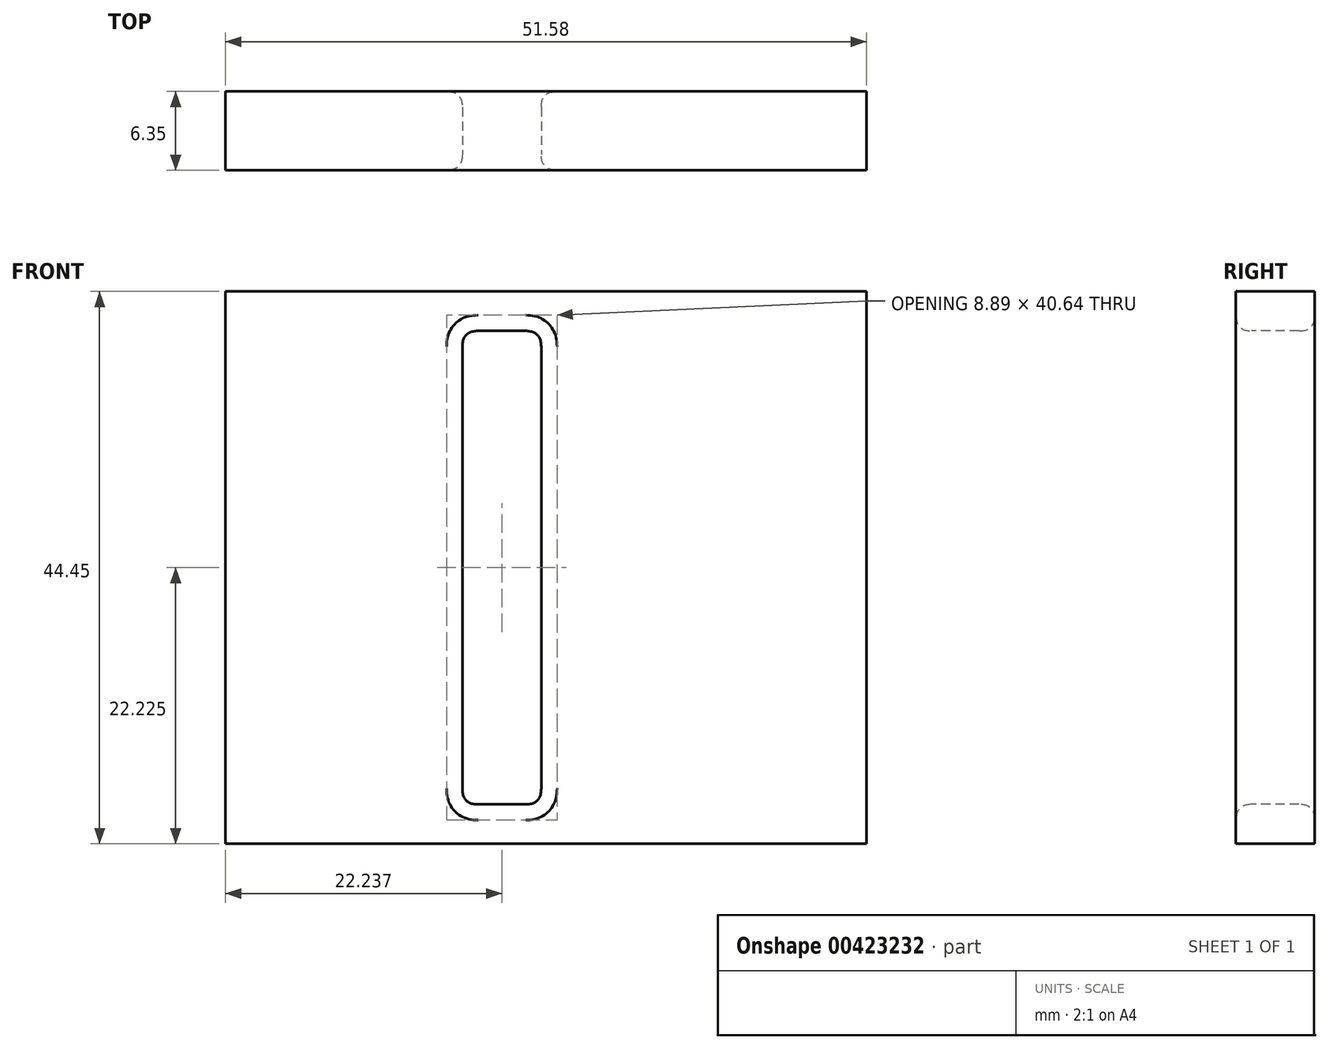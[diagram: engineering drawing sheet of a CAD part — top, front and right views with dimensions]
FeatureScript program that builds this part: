
annotation { "Feature Type Name" : "Feature", "Feature Type Description" : "" }
export const myFeature = defineFeature(function(context is Context, id is Id, definition is map)
    precondition{}
    {
        {
            var Q0;
            Q0=qCreatedBy(makeId("Front.planeOp"),FACE);
            var sketch = newSketch(context, id + "F0", { "sketchPlane" : qUnion([Q0])});
            skLineSegment(sketch, "E0.bottom", {"start": v(-46.53, 23.7) * mm, "end": v(5.05, 23.7) * mm});
            skLineSegment(sketch, "E0.top", {"start": v(-46.53, -20.74) * mm, "end": v(5.05, -20.74) * mm});
            skLineSegment(sketch, "E0.left", {"start": v(-46.53, 23.7) * mm, "end": v(-46.53, -20.74) * mm});
            skLineSegment(sketch, "E0.right", {"start": v(5.05, 23.7) * mm, "end": v(5.05, -20.74) * mm});
            skSolve(sketch);
        }
        {
            var Q0;
            Q0=makeQuery(id+"F0.imprint","IMPRINT",FACE,{"disambiguationData":[TD([[makeQuery(id+"F0.imprint","IMPRINT",EDGE,{"derivedFrom":sQuery(id+"F0.wireOp",EDGE,"E0.bottom")}),-1.0]])]});
            extrude(context, id + "F1", {"entities" : qUnion([Q0]), "depth" : 6.35 * mm, "offsetDistance" : 25.4 * mm});
        }
        {
            var Q0;
            Q0=makeQuery(id+"F1.opExtrude","CAP_FACE",FACE,{"disambiguationData":[OSD([sQuery(id+"F0.wireOp",EDGE,"E0.bottom"),sQuery(id+"F0.wireOp",EDGE,"E0.top"),sQuery(id+"F0.wireOp",EDGE,"E0.left"),sQuery(id+"F0.wireOp",EDGE,"E0.right")])],"isStart":false});
            var sketch = newSketch(context, id + "F2", { "sketchPlane" : qUnion([Q0])});
            skLineSegment(sketch, "E1", {"start": v(-41.45, -17.57) * mm, "end": v(-41.45, 20.53) * mm});
            skLineSegment(sketch, "E2", {"start": v(-41.45, 20.53) * mm, "end": v(-35.1, 20.53) * mm});
            skLineSegment(sketch, "E3", {"start": v(-35.1, 20.53) * mm, "end": v(-35.1, -17.57) * mm});
            skLineSegment(sketch, "E4.bottom", {"start": v(-27.47, 20.53) * mm, "end": v(-21.12, 20.53) * mm});
            skLineSegment(sketch, "E4.top", {"start": v(-27.47, -17.57) * mm, "end": v(-21.12, -17.57) * mm});
            skLineSegment(sketch, "E4.left", {"start": v(-27.47, 20.53) * mm, "end": v(-27.47, -17.57) * mm});
            skLineSegment(sketch, "E4.right", {"start": v(-21.12, 20.53) * mm, "end": v(-21.12, -17.57) * mm});
            skSolve(sketch);
        }
        {
            var Q0;
            Q0 = qSketchRegion(id + "F2", true);
            extrude(context, id + "F3", {"entities" : qUnion([Q0]), "operationType" : NewBodyOperationType.REMOVE, "oppositeDirection" : true, "depth" : 6.35 * mm, "offsetDistance" : 25.4 * mm});
        }
        {
            var Q0;
            Q0=makeQuery(id+"F3.boolean.opBoolean","COPY",FACE,{"derivedFrom":makeQuery(id+"F3.opExtrude","SWEPT_FACE",FACE,{"disambiguationData":[OSD([sQuery(id+"F2.wireOp",EDGE,"E4.left")])]})});
            var Q1;
            Q1=makeQuery(id+"F3.boolean.opBoolean","COPY",FACE,{"derivedFrom":makeQuery(id+"F3.opExtrude","SWEPT_FACE",FACE,{"disambiguationData":[OSD([sQuery(id+"F2.wireOp",EDGE,"E4.bottom")])]})});
            var Q2;
            Q2=makeQuery(id+"F3.boolean.opBoolean","COPY",FACE,{"derivedFrom":makeQuery(id+"F3.opExtrude","SWEPT_FACE",FACE,{"disambiguationData":[OSD([sQuery(id+"F2.wireOp",EDGE,"E4.right")])]})});
            var Q3;
            Q3=makeQuery(id+"F3.boolean.opBoolean","COPY",FACE,{"derivedFrom":makeQuery(id+"F3.opExtrude","SWEPT_FACE",FACE,{"disambiguationData":[OSD([sQuery(id+"F2.wireOp",EDGE,"E4.top")])]})});
            fillet(context, id + "F4", {"entities" : qUnion([Q0, Q1, Q2, Q3]), "crossSection" : FilletCrossSection.CONIC, "radius" : 1.27 * mm, "rho" : 0.5, "defaultsChanged" : false, "vertexSettings" : [], "allowEdgeOverflow" : false});
        }
    });
